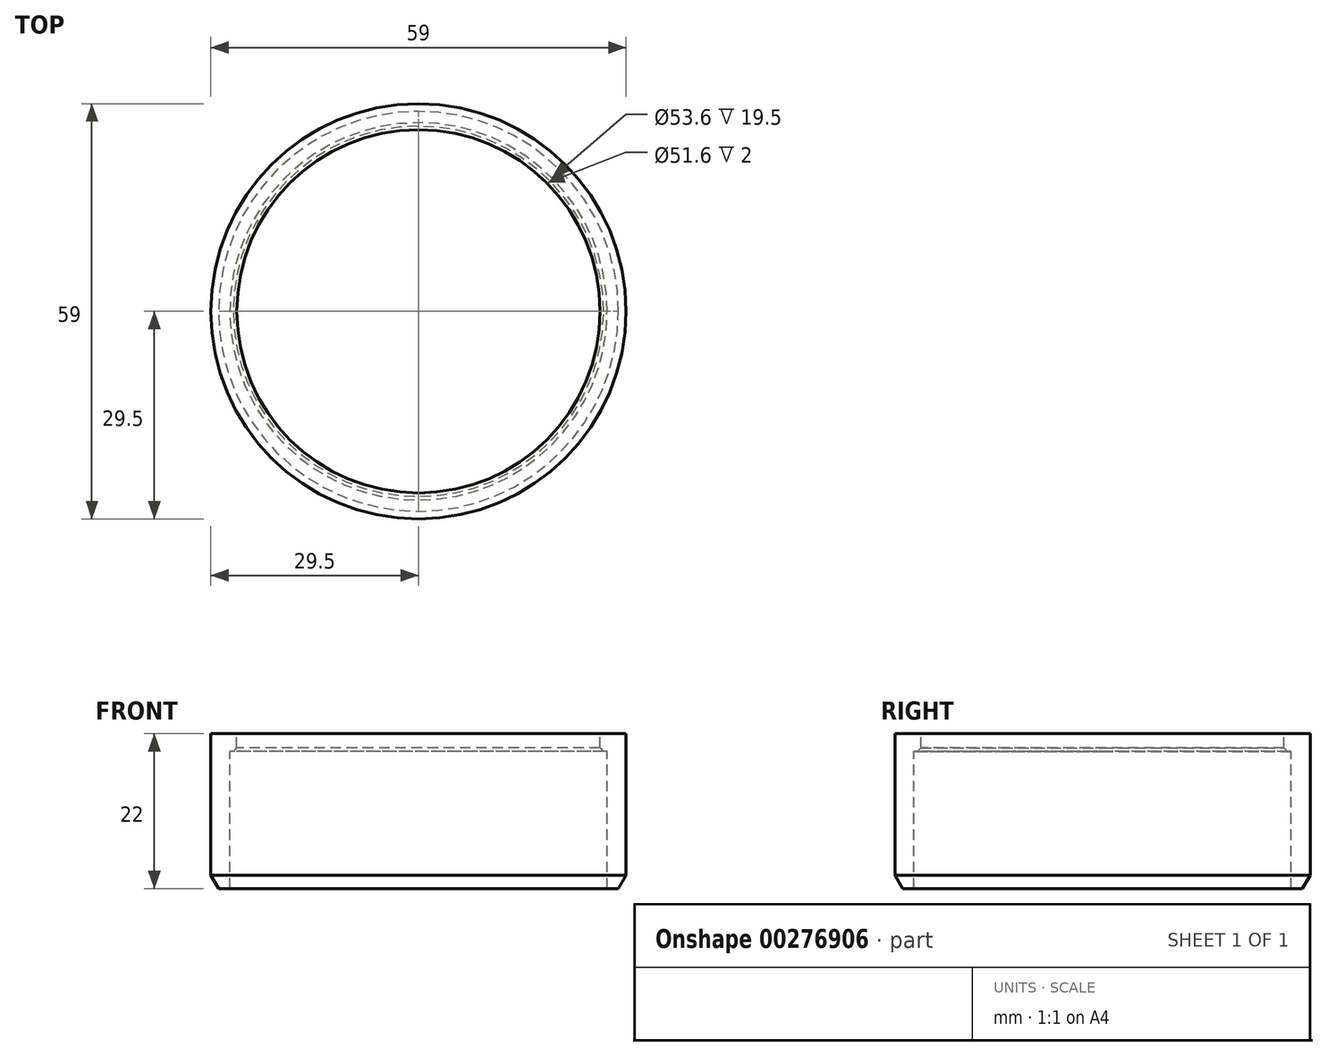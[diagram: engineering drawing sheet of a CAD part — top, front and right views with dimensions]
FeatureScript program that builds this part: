
annotation { "Feature Type Name" : "Feature", "Feature Type Description" : "" }
export const myFeature = defineFeature(function(context is Context, id is Id, definition is map)
    precondition{}
    {
        {
            var Q0;
            Q0=qCreatedBy(makeId("Front.planeOp"),FACE);
            var sketch = newSketch(context, id + "F0", { "sketchPlane" : qUnion([Q0])});
            skLineSegment(sketch, "E0", {"start": v(25.8, -13.37) * mm, "end": v(25.8, -15.37) * mm});
            skLineSegment(sketch, "E1", {"start": v(26.8, -15.87) * mm, "end": v(26.3, -15.87) * mm});
            skLineSegment(sketch, "E2", {"start": v(26.8, -15.87) * mm, "end": v(26.8, -35.37) * mm});
            skLineSegment(sketch, "E3", {"start": v(26.8, -35.37) * mm, "end": v(28.4, -35.37) * mm});
            skLineSegment(sketch, "E4", {"start": v(28.4, -35.37) * mm, "end": v(29.5, -33.46) * mm});
            skLineSegment(sketch, "E5", {"start": v(29.5, -33.46) * mm, "end": v(29.5, -13.37) * mm});
            skLineSegment(sketch, "E6", {"start": v(29.5, -13.37) * mm, "end": v(25.8, -13.37) * mm});
            skLineSegment(sketch, "E7", {"start": v(0, 24.42) * mm, "end": v(0, -13.18) * mm, "construction": true});
            skLineSegment(sketch, "E8", {"start": v(26.3, -15.87) * mm, "end": v(25.8, -15.37) * mm});
            skPoint(sketch, "E9.orphan", {"position": v(25.8, -15.87) * mm});
            skSolve(sketch);
        }
        {
            var Q0;
            Q0=makeQuery(id+"F0.imprint","IMPRINT",FACE,{"disambiguationData":[TD([[makeQuery(id+"F0.imprint","IMPRINT",EDGE,{"derivedFrom":sQuery(id+"F0.wireOp",EDGE,"E0")}),1.0]])]});
            var Q1;
            Q1=sQuery(id+"F0.wireOp",EDGE,"E7");
            revolve(context, id + "F1", {"entities" : qUnion([Q0]), "axis" : qUnion([Q1]), "revolveType" : RevolveType.FULL});
        }
    });
